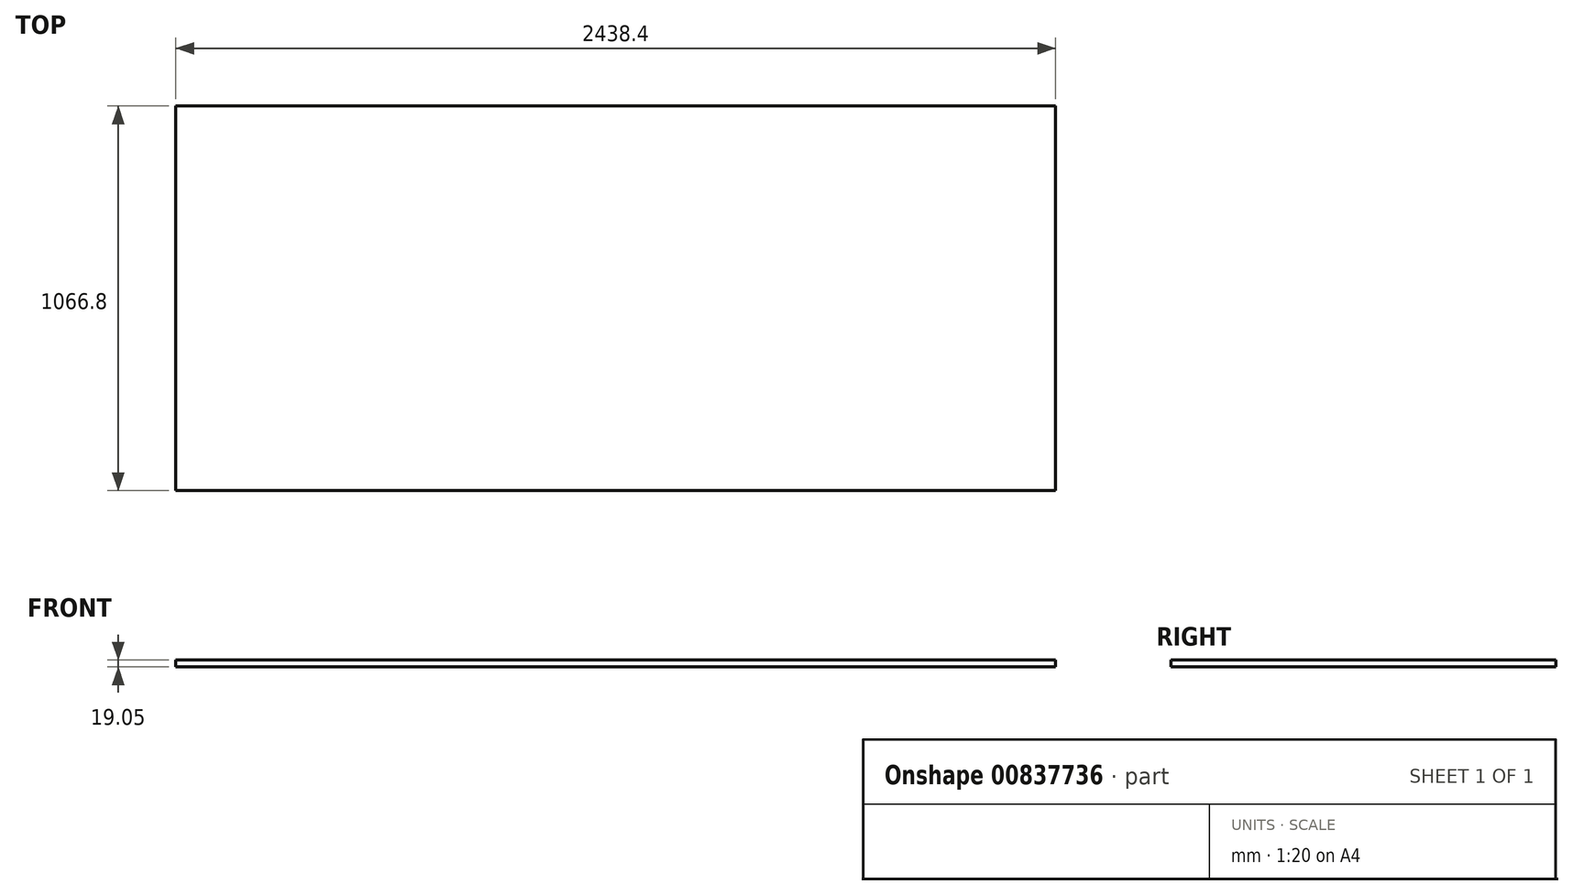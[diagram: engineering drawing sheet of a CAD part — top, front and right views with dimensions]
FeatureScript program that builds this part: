
annotation { "Feature Type Name" : "Feature", "Feature Type Description" : "" }
export const myFeature = defineFeature(function(context is Context, id is Id, definition is map)
    precondition{}
    {
        {
            var Q0;
            Q0=qCreatedBy(makeId("Top.planeOp"),FACE);
            var sketch = newSketch(context, id + "F0", { "sketchPlane" : qUnion([Q0])});
            skLineSegment(sketch, "E0.bottom", {"start": v(0, 0) * mm, "end": v(2438.4, 0) * mm});
            skLineSegment(sketch, "E0.top", {"start": v(0, 1066.8) * mm, "end": v(2438.4, 1066.8) * mm});
            skLineSegment(sketch, "E0.left", {"start": v(0, 0) * mm, "end": v(0, 1066.8) * mm});
            skLineSegment(sketch, "E0.right", {"start": v(2438.4, 0) * mm, "end": v(2438.4, 1066.8) * mm});
            skSolve(sketch);
        }
        {
            var Q0;
            Q0=makeQuery(id+"F0.imprint","IMPRINT",FACE,{"disambiguationData":[TD([[makeQuery(id+"F0.imprint","IMPRINT",EDGE,{"derivedFrom":sQuery(id+"F0.wireOp",EDGE,"E0.bottom")}),1.0]])]});
            extrude(context, id + "F1", {"entities" : qUnion([Q0]), "depth" : 19.05 * mm, "offsetDistance" : 25.4 * mm});
        }
    });
